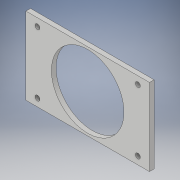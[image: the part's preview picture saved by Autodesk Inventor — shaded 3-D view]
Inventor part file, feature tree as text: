
AUTODESK INVENTOR PART (.ipt)
format: ipt  version: 2019 (Build 230136000, 136)  size: 132,608 bytes
history: native  units: mm
features: sketch x3, extrude x2, other x1, hole x1
ambient origin geometry x8: Origin, YZ Plane, XZ Plane, XY Plane, X Axis, Y Axis, Z Axis, Center Point
bodies: Body1 (feature_tree)
feature tree (7):
  other  "ソリッド1"
  extrude  "押し出し1"  Depth=80.0mm
  extrude  "押し出し2"  Depth=50.0mm
  hole  "穴1"  [1 undecoded]
  sketch  "スケッチ1"
  sketch  "スケッチ2"
  sketch  "スケッチ3"
note: 1 required parameter value undecoded (feature->parameter linkage not recoverable at this tier; creation-order binding heuristic only, values carry confidence <= 0.55)
